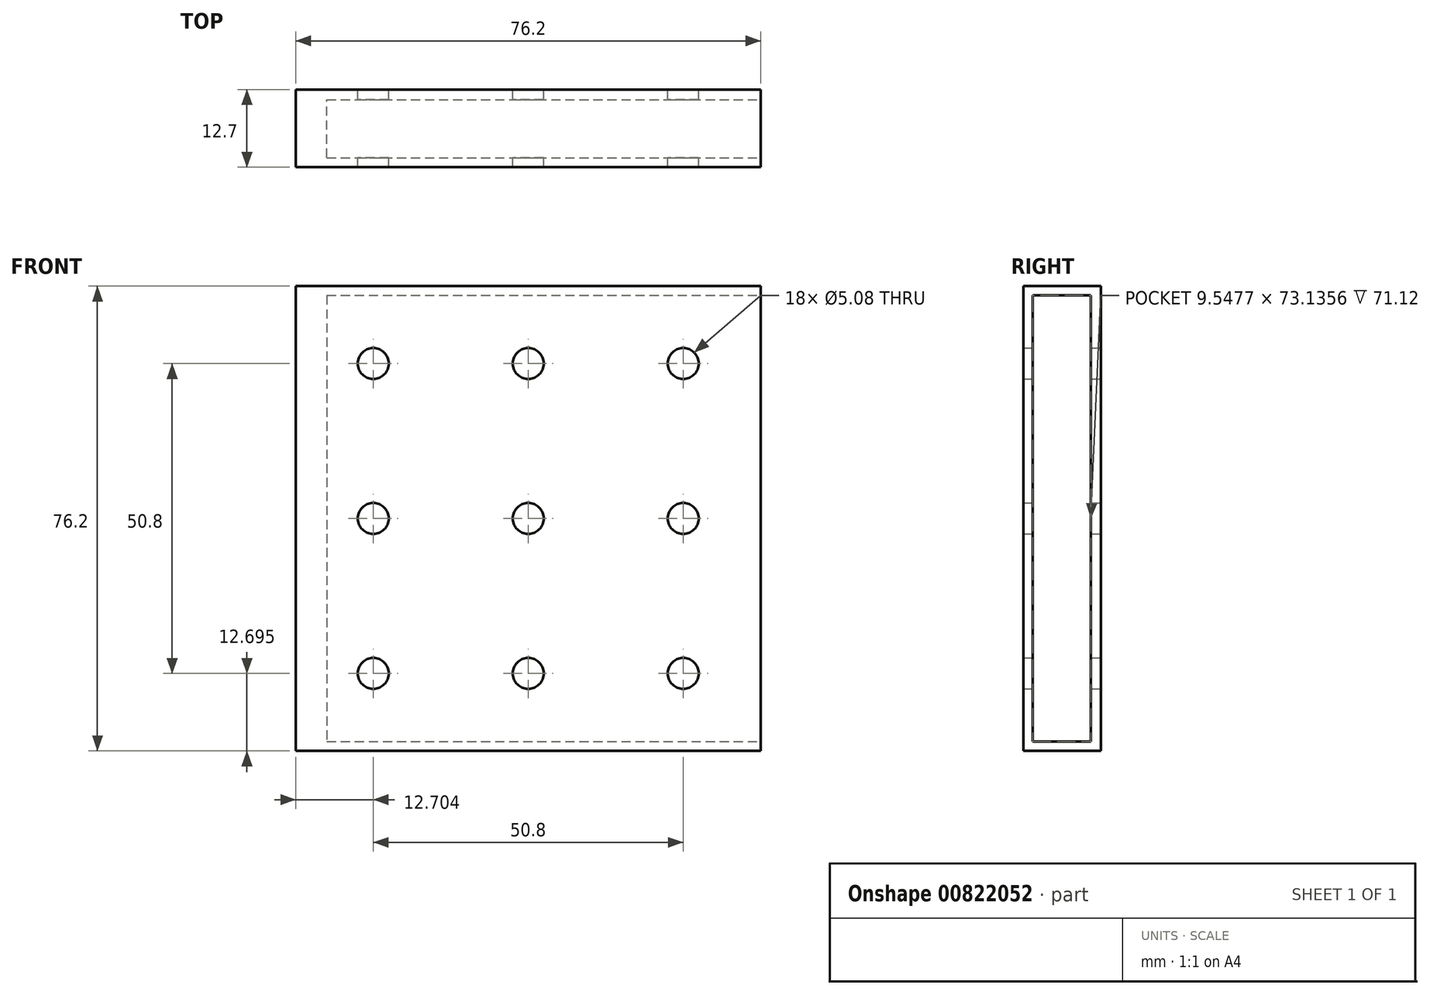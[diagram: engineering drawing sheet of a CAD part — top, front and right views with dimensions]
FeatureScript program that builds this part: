
annotation { "Feature Type Name" : "Feature", "Feature Type Description" : "" }
export const myFeature = defineFeature(function(context is Context, id is Id, definition is map)
    precondition{}
    {
        {
            var Q0;
            Q0=qCreatedBy(makeId("Front.planeOp"),FACE);
            var sketch = newSketch(context, id + "F0", { "sketchPlane" : qUnion([Q0])});
            skLineSegment(sketch, "E0", {"start": v(-44.2, 40.2) * mm, "end": v(-44.2, 14.8) * mm});
            skLineSegment(sketch, "E1", {"start": v(-44.2, 14.8) * mm, "end": v(-40.77, 14.8) * mm});
            skLineSegment(sketch, "E2", {"start": v(-40.77, 14.8) * mm, "end": v(-44.2, 14.8) * mm});
            skLineSegment(sketch, "E3", {"start": v(-44.2, 14.8) * mm, "end": v(-44.2, -10.6) * mm});
            skLineSegment(sketch, "E4", {"start": v(-44.2, -10.6) * mm, "end": v(-44.2, -36) * mm});
            skLineSegment(sketch, "E5", {"start": v(-44.2, -36) * mm, "end": v(-18.8, -36) * mm});
            skLineSegment(sketch, "E6", {"start": v(-18.8, -36) * mm, "end": v(6.6, -36) * mm});
            skLineSegment(sketch, "E7", {"start": v(6.6, -36) * mm, "end": v(32, -36) * mm});
            skLineSegment(sketch, "E8", {"start": v(32, -36) * mm, "end": v(32, 40.2) * mm});
            skLineSegment(sketch, "E9", {"start": v(32, 40.2) * mm, "end": v(-44.2, 40.2) * mm});
            skLineSegment(sketch, "E10", {"start": v(-40.77, 14.8) * mm, "end": v(32, 14.8) * mm});
            skLineSegment(sketch, "E11", {"start": v(-44.2, -10.6) * mm, "end": v(32, -10.6) * mm});
            skLineSegment(sketch, "E12", {"start": v(-18.8, -36) * mm, "end": v(-18.8, 40.2) * mm});
            skLineSegment(sketch, "E13", {"start": v(6.6, -36) * mm, "end": v(6.6, 40.2) * mm});
            skPoint(sketch, "E14.startSnap0", {"position": v(-6.1, 40.2) * mm});
            skCircle(sketch, "E15", {"center": v(-6.1, 27.5) * mm, "radius": 2.54 * mm});
            skCircle(sketch, "E16", {"center": v(19.3, 27.5) * mm, "radius": 2.54 * mm});
            skCircle(sketch, "E17", {"center": v(-31.5, 27.5) * mm, "radius": 2.54 * mm});
            skCircle(sketch, "E18", {"center": v(-31.5, 2.1) * mm, "radius": 2.54 * mm});
            skCircle(sketch, "E19", {"center": v(-6.1, 2.1) * mm, "radius": 2.54 * mm});
            skCircle(sketch, "E20", {"center": v(19.3, 2.1) * mm, "radius": 2.54 * mm});
            skCircle(sketch, "E21", {"center": v(19.3, -23.3) * mm, "radius": 2.54 * mm});
            skCircle(sketch, "E22", {"center": v(-6.1, -23.3) * mm, "radius": 2.54 * mm});
            skCircle(sketch, "E23", {"center": v(-31.5, -23.3) * mm, "radius": 2.54 * mm});
            skSolve(sketch);
        }
        {
            var Q0;
            Q0=qSketchRegion(id+"F0",true);
            var Q1;
            Q1=makeQuery(id+"F0.imprint","IMPRINT",FACE,{"disambiguationData":[TD([[makeQuery(id+"F0.imprint","IMPRINT",EDGE,{"derivedFrom":sQuery(id+"F0.wireOp",EDGE,"E19")}),-1.0]])]});
            extrude(context, id + "F1", {"entities" : qUnion([Q0, Q1]), "depth" : 12.7 * mm, "offsetDistance" : 25.4 * mm});
        }
        {
            var Q0;
            Q0=makeQuery(id+"F1.opExtrude","SWEPT_FACE",FACE,{"disambiguationData":[OSD([sQuery(id+"F0.wireOp",EDGE,"E8")])]});
            var sketch = newSketch(context, id + "F2", { "sketchPlane" : qUnion([Q0])});
            skLineSegment(sketch, "E24.bottom", {"start": v(-11.17, 38.67) * mm, "end": v(-1.62, 38.67) * mm});
            skLineSegment(sketch, "E24.top", {"start": v(-11.17, -34.47) * mm, "end": v(-1.62, -34.47) * mm});
            skLineSegment(sketch, "E24.left", {"start": v(-11.17, 38.67) * mm, "end": v(-11.17, -34.47) * mm});
            skLineSegment(sketch, "E24.right", {"start": v(-1.62, 38.67) * mm, "end": v(-1.62, -34.47) * mm});
            skSolve(sketch);
        }
        {
            var Q0;
            Q0=qSketchRegion(id+"F2",true);
            extrude(context, id + "F3", {"entities" : qUnion([Q0]), "operationType" : NewBodyOperationType.REMOVE, "oppositeDirection" : true, "depth" : 71.12 * mm, "offsetDistance" : 25.4 * mm});
        }
    });
